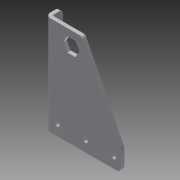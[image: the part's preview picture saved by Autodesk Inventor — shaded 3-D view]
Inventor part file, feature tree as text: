
AUTODESK INVENTOR PART (.ipt)
format: ipt  version: 2014 (Build 180170000, 170)  size: 164,864 bytes
history: native  units: in
note: dims shown in document units (in); Inventor stores cm internally (conversion verified against a paired STEP export)
features: sheet_metal_op x4, other x3, sketch x2, fillet x1
ambient origin geometry x8: Origin, YZ Plane, XZ Plane, XY Plane, X Axis, Y Axis, Z Axis, Center Point
bodies: Solid1 (feature_tree)
feature tree (10):
  sheet_metal_op  "Face1"
  sheet_metal_op  "Flange2"
  fillet  "Fillet1"  Radius=0.125in
  sketch  "Sketch1"  dims[d5=2.5in d6=0.163in d7=0.25in d8=0.375in d11=0.125in]
  other  "Plate1"
  sketch  "Sketch3"  dims[d22=1.1811in d24=1.0in d25=0.3937in d27=1.0in d29=3.5in d30=0.75in d31=1.125in d32=0.5in d34=0.75in d35=0.5in d36=0.125in d37=0.0625in d38=0.25in d39=0.125in d40=0.5in d41=90.0deg d42=0.05in d43=0.5in d44=0.125in d45=0.125in d46=0.125in]
  other  "Plate3"
  sheet_metal_op  "Bend2"
  sheet_metal_op  "Corner2"
  other  "Definition1"
